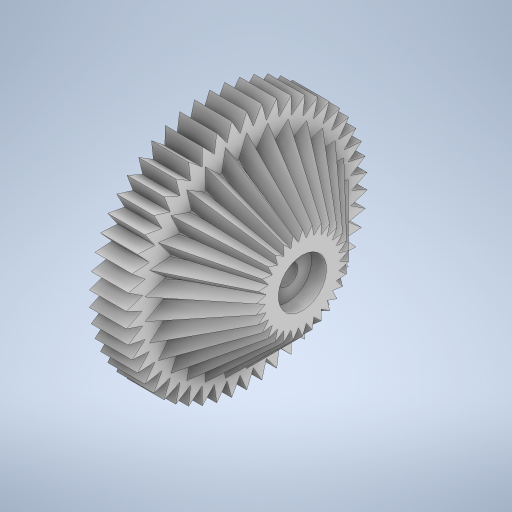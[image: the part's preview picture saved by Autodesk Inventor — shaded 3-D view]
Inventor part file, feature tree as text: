
AUTODESK INVENTOR PART (.ipt)
format: ipt  version: 2023 (Build 270158030, 158C)  size: 554,496 bytes
history: native  units: in
note: dims shown in document units (in); Inventor stores cm internally (conversion verified against a paired STEP export)
features: sketch x7, extrude x4, pattern_circular x2, other x1, loft x1
ambient origin geometry x8: Origin, YZ Plane, XZ Plane, XY Plane, X Axis, Y Axis, Z Axis, Center Point
bodies: Solid1 (feature_tree)
feature tree (15):
  other  "Main Body"
  loft  "Loft3"
  pattern_circular  "Circular Pattern4"  Count=2  [1 undecoded]
  extrude  "Extrusion7"  Depth=1.9685in
  extrude  "Extrusion8"  Depth=0.3937in
  extrude  "Extrusion9"  Depth=0.3937in
  extrude  "Extrusion10"  TaperAngle=0.0deg  [1 undecoded]
  pattern_circular  "Circular Pattern5"  Count=30 Angle=360.0deg
  sketch  "Sketch1"  dims[d1=45.0deg d2=1.1811in]
  sketch  "Sketch16"  dims[d4=90.0deg d50=0.7874in]
  sketch  "Sketch17"  dims[d51=0.3937in d52=1.9685in]
  sketch  "Sketch18"  dims[d53=45.0deg d54=0.3937in]
  sketch  "Sketch19"  dims[d55=45.0deg d56=0.3937in]
  sketch  "Sketch20"  dims[d57=0.0in d58=90.0deg d59=0.0in d60=90.0deg d61=11.811in d62=360.0deg]
  sketch  "Sketch21"  dims[d64=1.0236in d65=0.315in d66=0.0in d67=0.4331in d68=0.0in d69=0.0in d70=1.0236in d71=0.315in d72=0.0in d73=0.3937in d74=45.0deg d75=0.315in d76=0.0in d77=19.685in d78=360.0deg d39=0.0197in d40=0.0344in d41=0.0197in d42=0.0344in]
note: 2 required parameter values undecoded (feature->parameter linkage not recoverable at this tier; creation-order binding heuristic only, values carry confidence <= 0.55)
